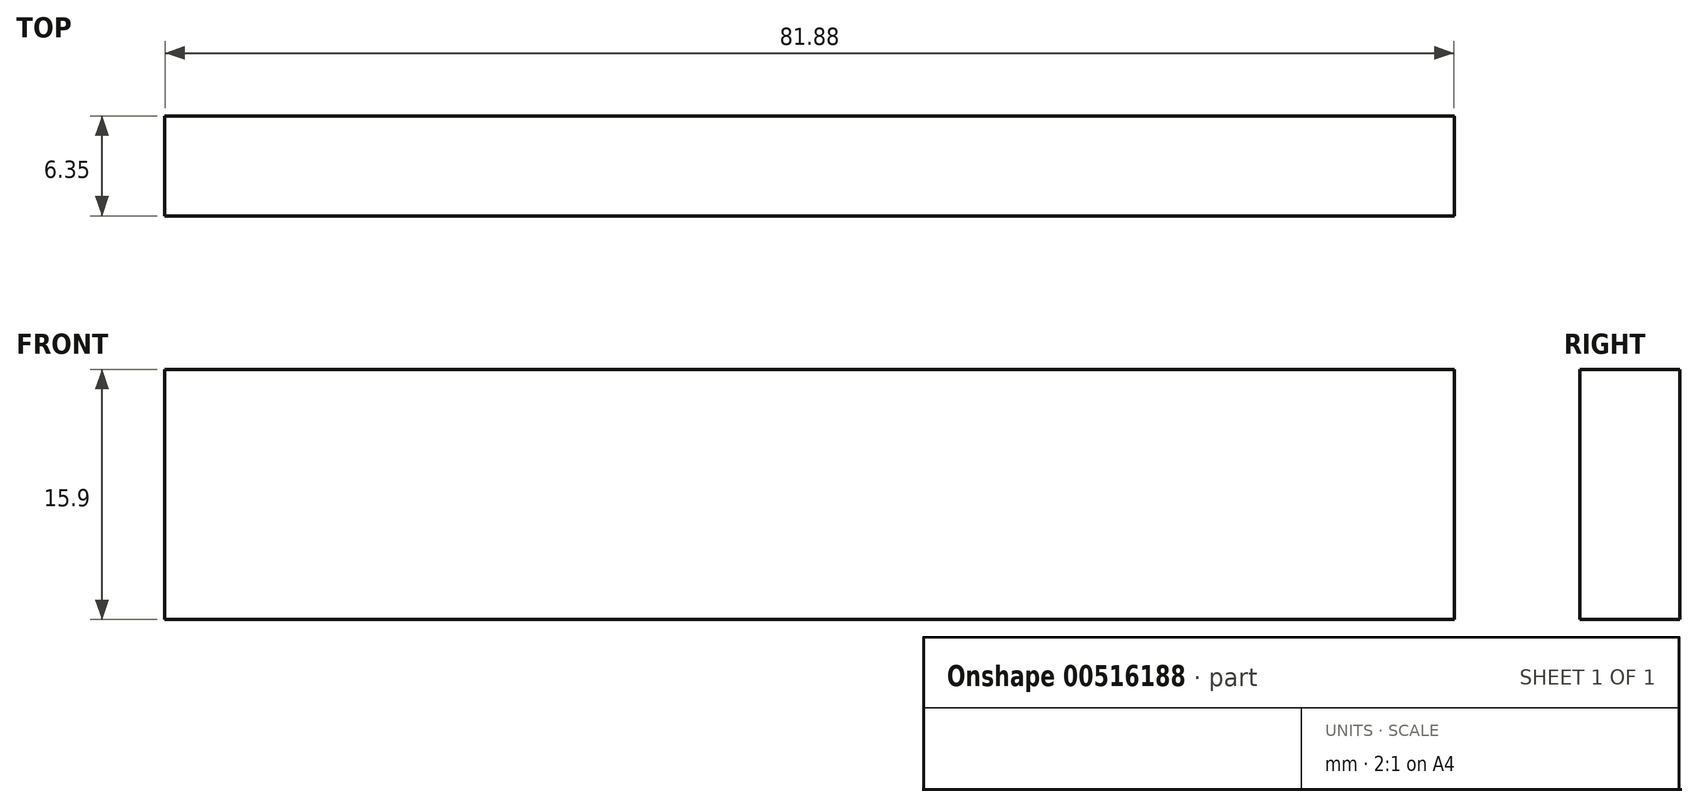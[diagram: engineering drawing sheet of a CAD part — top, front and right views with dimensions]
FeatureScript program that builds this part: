
annotation { "Feature Type Name" : "Feature", "Feature Type Description" : "" }
export const myFeature = defineFeature(function(context is Context, id is Id, definition is map)
    precondition{}
    {
        {
            var Q0;
            Q0=qCreatedBy(makeId("Front.planeOp"),FACE);
            var sketch = newSketch(context, id + "F0", { "sketchPlane" : qUnion([Q0])});
            skLineSegment(sketch, "E0.bottom", {"start": v(40.94, -7.95) * mm, "end": v(-40.94, -7.95) * mm});
            skLineSegment(sketch, "E0.top", {"start": v(40.94, 7.95) * mm, "end": v(-40.94, 7.95) * mm});
            skLineSegment(sketch, "E0.left", {"start": v(40.94, -7.95) * mm, "end": v(40.94, 7.95) * mm});
            skLineSegment(sketch, "E0.right", {"start": v(-40.94, -7.95) * mm, "end": v(-40.94, 7.95) * mm});
            skPoint(sketch, "E0.middle", {"position": v(0, 0) * mm});
            skSolve(sketch);
        }
        {
            var Q0;
            Q0=makeQuery(id+"F0.imprint","IMPRINT",FACE,{"disambiguationData":[TD([[makeQuery(id+"F0.imprint","IMPRINT",EDGE,{"derivedFrom":sQuery(id+"F0.wireOp",EDGE,"E0.bottom")}),-1.0]])]});
            extrude(context, id + "F1", {"entities" : qUnion([Q0]), "depth" : 6.35 * mm});
        }
    });
